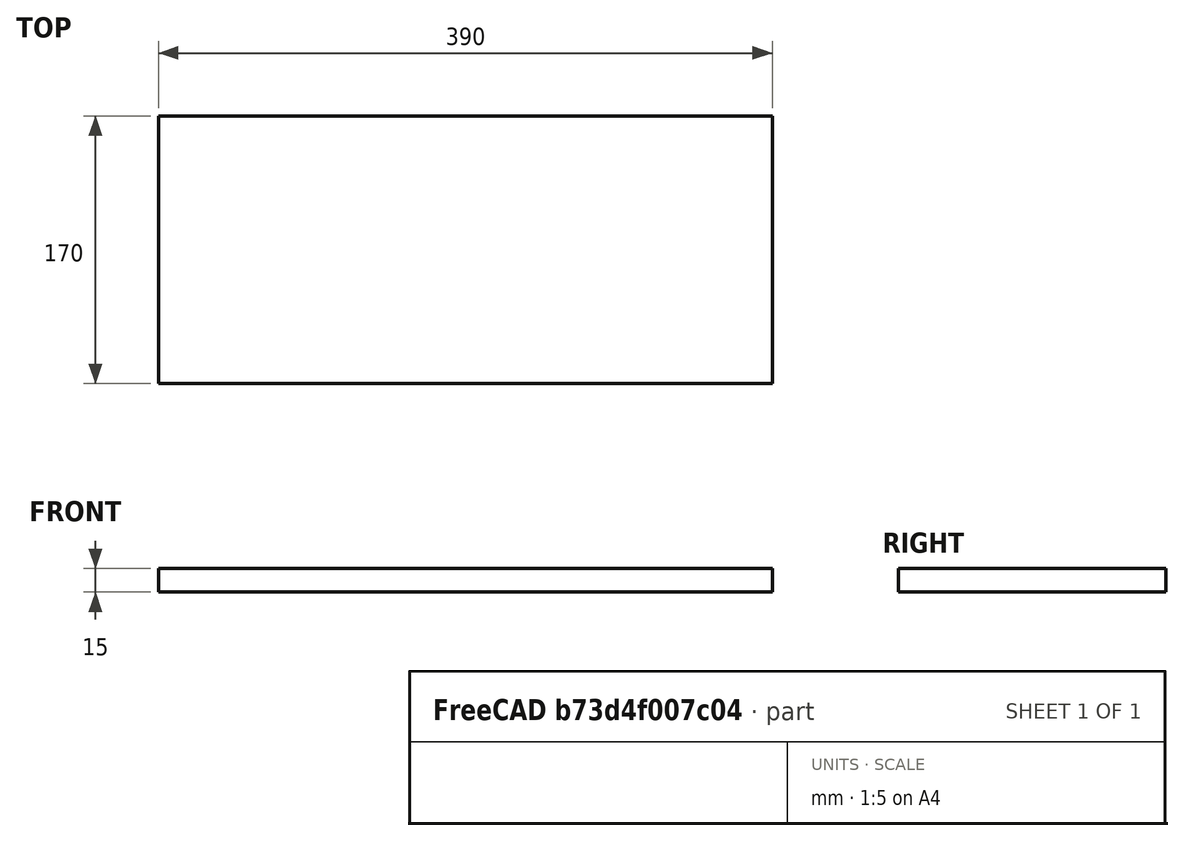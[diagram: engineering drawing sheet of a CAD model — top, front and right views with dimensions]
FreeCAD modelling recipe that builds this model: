
FCSTD DOCUMENT  (FreeCAD 0.18R4 (GitTag))
Label: MidBaseBig
License: All rights reserved
LicenseURL: http://en.wikipedia.org/wiki/All_rights_reserved
objects: Sketcher::SketchObject×1, PartDesign::Pad×1, PartDesign::Body×1
note: 4 computed .brp shape members not serialized (recipe doc carries the construction recipe); baked Part::Feature solids carry a one-line shape summary decoded from their .brp

FEATURE [Sketcher::SketchObject] Sketch
  MapMode = 5
  Support = -> [XY_Plane]
  sketch-geometry (4):
    g0: LineSegment StartX=0 StartY=0 StartZ=0 EndX=-390 EndY=0 EndZ=0
    g1: LineSegment StartX=-390 StartY=0 StartZ=0 EndX=-390 EndY=170 EndZ=0
    g2: LineSegment StartX=-390 StartY=170 StartZ=0 EndX=0 EndY=170 EndZ=0
    g3: LineSegment StartX=0 StartY=170 StartZ=0 EndX=0 EndY=0 EndZ=0
  constraints (11):
    c: Coincident(g0,g1)
    c: Coincident(g1,g2)
    c: Coincident(g2,g3)
    c: Coincident(g3,g0)
    c: Horizontal(g0)
    c: Horizontal(g2)
    c: Vertical(g1)
    c: Vertical(g3)
    c: Distance(g2) = 390
    c: Distance(g3) = 170
    c: Coincident(g0,g-1)
FEATURE [PartDesign::Pad] Pad
  Length = 15
  Length2 = 100
  Profile = -> Sketch
  Type = 0
FEATURE [PartDesign::Body] Body
  Group = -> [Sketch,Pad]
  Origin = -> Origin
  Tip = -> Pad
